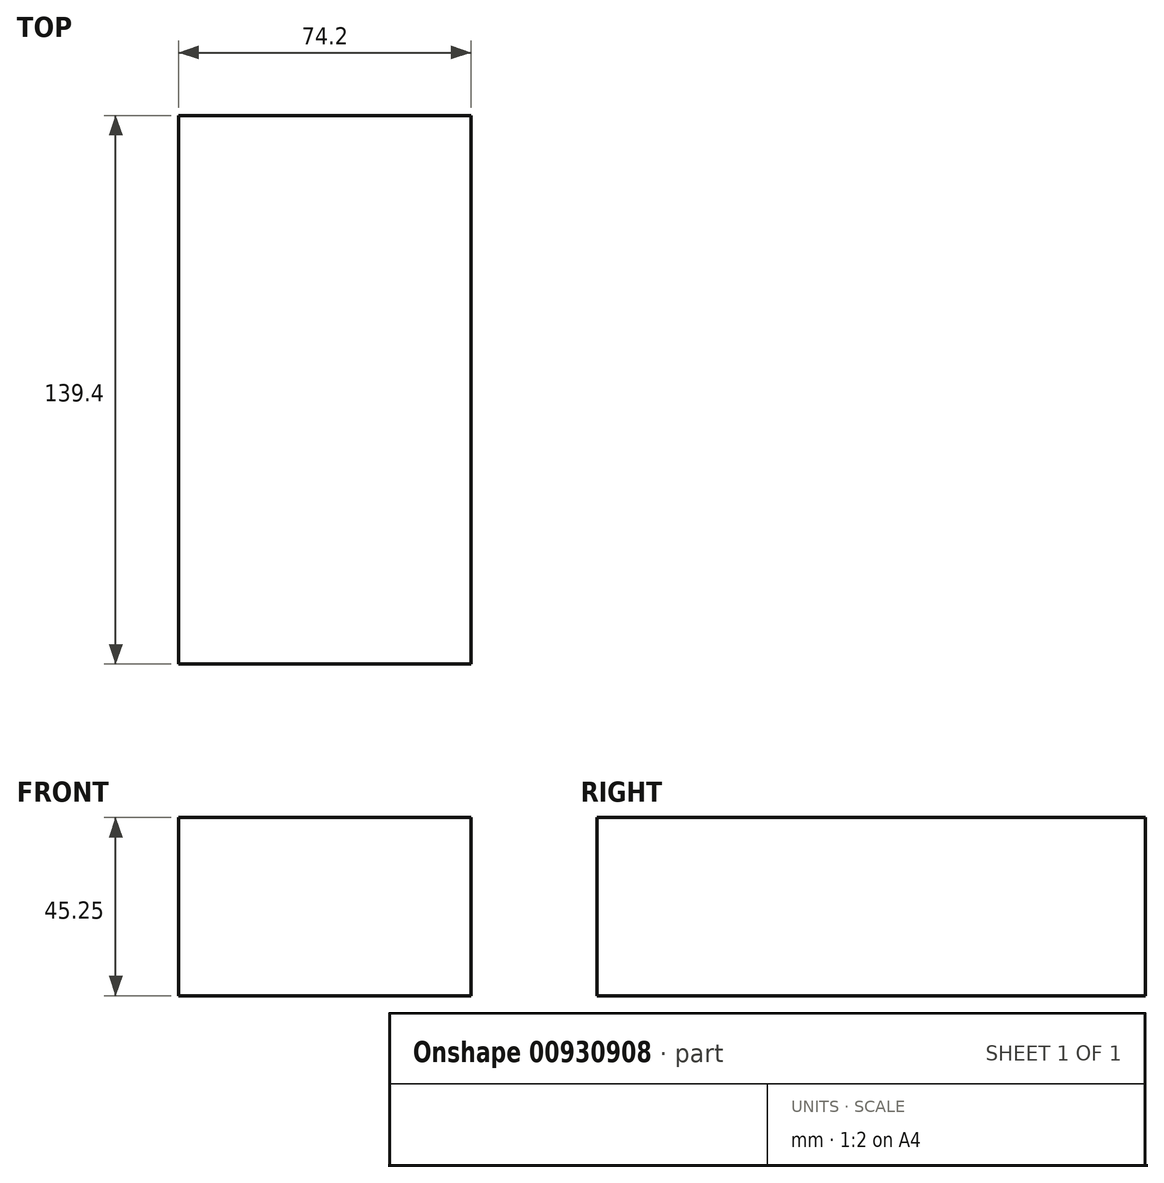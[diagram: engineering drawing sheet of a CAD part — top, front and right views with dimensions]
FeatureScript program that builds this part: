
annotation { "Feature Type Name" : "Feature", "Feature Type Description" : "" }
export const myFeature = defineFeature(function(context is Context, id is Id, definition is map)
    precondition{}
    {
        {
            var Q0;
            Q0=qCreatedBy(makeId("Front.planeOp"),FACE);
            var sketch = newSketch(context, id + "F0", { "sketchPlane" : qUnion([Q0])});
            skLineSegment(sketch, "E0.bottom", {"start": v(-154.17, 37.24) * mm, "end": v(-79.97, 37.24) * mm});
            skLineSegment(sketch, "E0.top", {"start": v(-154.17, -8.01) * mm, "end": v(-79.97, -8.01) * mm});
            skLineSegment(sketch, "E0.left", {"start": v(-154.17, 37.24) * mm, "end": v(-154.17, -8.01) * mm});
            skLineSegment(sketch, "E0.right", {"start": v(-79.97, 37.24) * mm, "end": v(-79.97, -8.01) * mm});
            skSolve(sketch);
        }
        {
            var Q0;
            Q0=sQuery(id+"F0.wireOp",EDGE,"E0.left");
            var Q1;
            Q1=sQuery(id+"F0.wireOp",EDGE,"E0.bottom");
            var Q2;
            Q2=sQuery(id+"F0.wireOp",EDGE,"E0.right");
            var Q3;
            Q3=sQuery(id+"F0.wireOp",EDGE,"E0.top");
            extrude(context, id + "F1", {"bodyType" : ToolBodyType.SURFACE, "surfaceEntities" : qUnion([Q0, Q1, Q2, Q3]), "depth" : 114.4 * mm, "offsetDistance" : 25 * mm, "hasSecondDirection" : true, "secondDirectionOppositeDirection" : true, "secondDirectionDepth" : 25 * mm});
        }
        {
            var Q0;
            Q0=qCreatedBy(makeId("Front.planeOp"),FACE);
            cPlane(context, id + "F2", {"entities" : qUnion([Q0]), "cplaneType" : CPlaneType.OFFSET, "offset" : 192 * mm, "width" : 150 * mm, "height" : 150 * mm});
        }
    });
